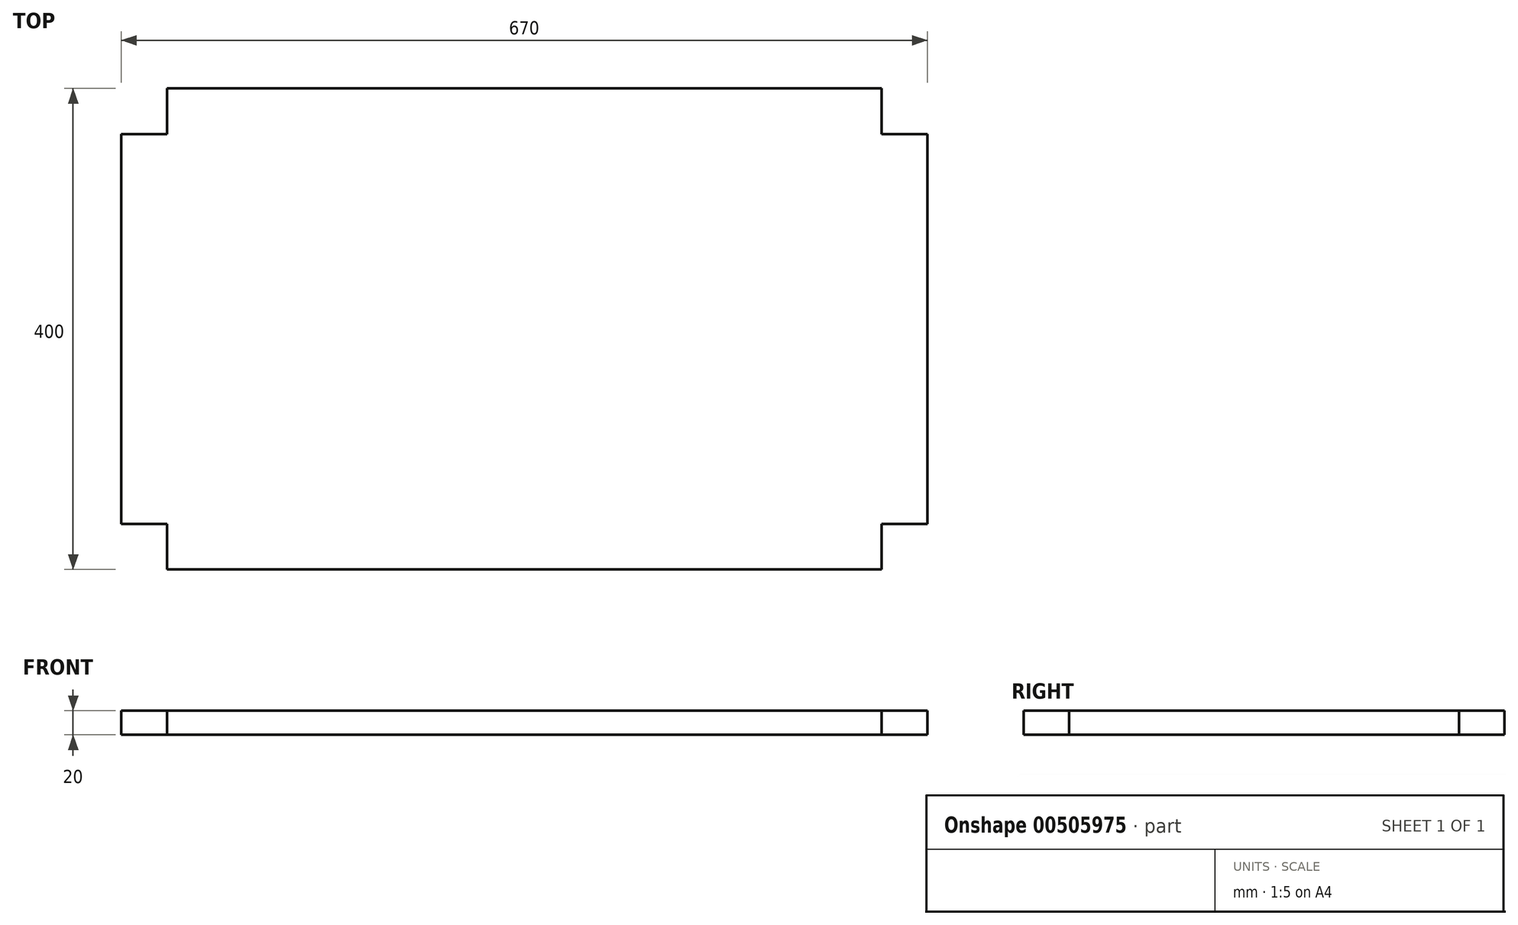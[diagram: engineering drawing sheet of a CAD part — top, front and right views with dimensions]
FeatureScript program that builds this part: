
annotation { "Feature Type Name" : "Feature", "Feature Type Description" : "" }
export const myFeature = defineFeature(function(context is Context, id is Id, definition is map)
    precondition{}
    {
        {
            var Q0;
            Q0=qCreatedBy(makeId("Top.planeOp"),FACE);
            var sketch = newSketch(context, id + "F0", { "sketchPlane" : qUnion([Q0])});
            skLineSegment(sketch, "E0.bottom", {"start": v(-466.17, 317.6) * mm, "end": v(203.83, 317.6) * mm});
            skLineSegment(sketch, "E0.top", {"start": v(-466.17, -82.4) * mm, "end": v(203.83, -82.4) * mm});
            skLineSegment(sketch, "E0.left", {"start": v(-466.17, 317.6) * mm, "end": v(-466.17, -82.4) * mm});
            skLineSegment(sketch, "E0.right", {"start": v(203.83, 317.6) * mm, "end": v(203.83, -82.4) * mm});
            skSolve(sketch);
        }
        {
            var Q0;
            Q0 = qSketchRegion(id + "F0", true);
            extrude(context, id + "F1", {"entities" : qUnion([Q0]), "depth" : 20 * mm, "offsetDistance" : 25 * mm});
        }
        {
            var Q0;
            Q0=makeQuery(id+"F1.opExtrude","CAP_FACE",FACE,{"disambiguationData":[OSD([sQuery(id+"F0.wireOp",EDGE,"E0.bottom"),sQuery(id+"F0.wireOp",EDGE,"E0.top"),sQuery(id+"F0.wireOp",EDGE,"E0.left"),sQuery(id+"F0.wireOp",EDGE,"E0.right")])],"isStart":false});
            var sketch = newSketch(context, id + "F2", { "sketchPlane" : qUnion([Q0])});
            skLineSegment(sketch, "E1.bottom", {"start": v(-466.17, 317.6) * mm, "end": v(-428.17, 317.6) * mm});
            skLineSegment(sketch, "E1.top", {"start": v(-466.17, 279.6) * mm, "end": v(-428.17, 279.6) * mm});
            skLineSegment(sketch, "E1.left", {"start": v(-466.17, 317.6) * mm, "end": v(-466.17, 279.6) * mm});
            skLineSegment(sketch, "E1.right", {"start": v(-428.17, 317.6) * mm, "end": v(-428.17, 279.6) * mm});
            skLineSegment(sketch, "E2.bottom", {"start": v(-466.17, -82.4) * mm, "end": v(-428.17, -82.4) * mm});
            skLineSegment(sketch, "E2.top", {"start": v(-466.17, -44.4) * mm, "end": v(-428.17, -44.4) * mm});
            skLineSegment(sketch, "E2.left", {"start": v(-466.17, -82.4) * mm, "end": v(-466.17, -44.4) * mm});
            skLineSegment(sketch, "E2.right", {"start": v(-428.17, -82.4) * mm, "end": v(-428.17, -44.4) * mm});
            skLineSegment(sketch, "E3.bottom", {"start": v(203.83, 317.6) * mm, "end": v(165.83, 317.6) * mm});
            skLineSegment(sketch, "E3.top", {"start": v(203.83, 279.6) * mm, "end": v(165.83, 279.6) * mm});
            skLineSegment(sketch, "E3.left", {"start": v(203.83, 317.6) * mm, "end": v(203.83, 279.6) * mm});
            skLineSegment(sketch, "E3.right", {"start": v(165.83, 317.6) * mm, "end": v(165.83, 279.6) * mm});
            skLineSegment(sketch, "E4.bottom", {"start": v(203.83, -82.4) * mm, "end": v(165.83, -82.4) * mm});
            skLineSegment(sketch, "E4.top", {"start": v(203.83, -44.4) * mm, "end": v(165.83, -44.4) * mm});
            skLineSegment(sketch, "E4.left", {"start": v(203.83, -82.4) * mm, "end": v(203.83, -44.4) * mm});
            skLineSegment(sketch, "E4.right", {"start": v(165.83, -82.4) * mm, "end": v(165.83, -44.4) * mm});
            skSolve(sketch);
        }
        {
            var Q0;
            Q0 = qSketchRegion(id + "F2", true);
            extrude(context, id + "F3", {"entities" : qUnion([Q0]), "operationType" : NewBodyOperationType.REMOVE, "oppositeDirection" : true, "depth" : 25 * mm, "offsetDistance" : 25 * mm});
        }
    });
